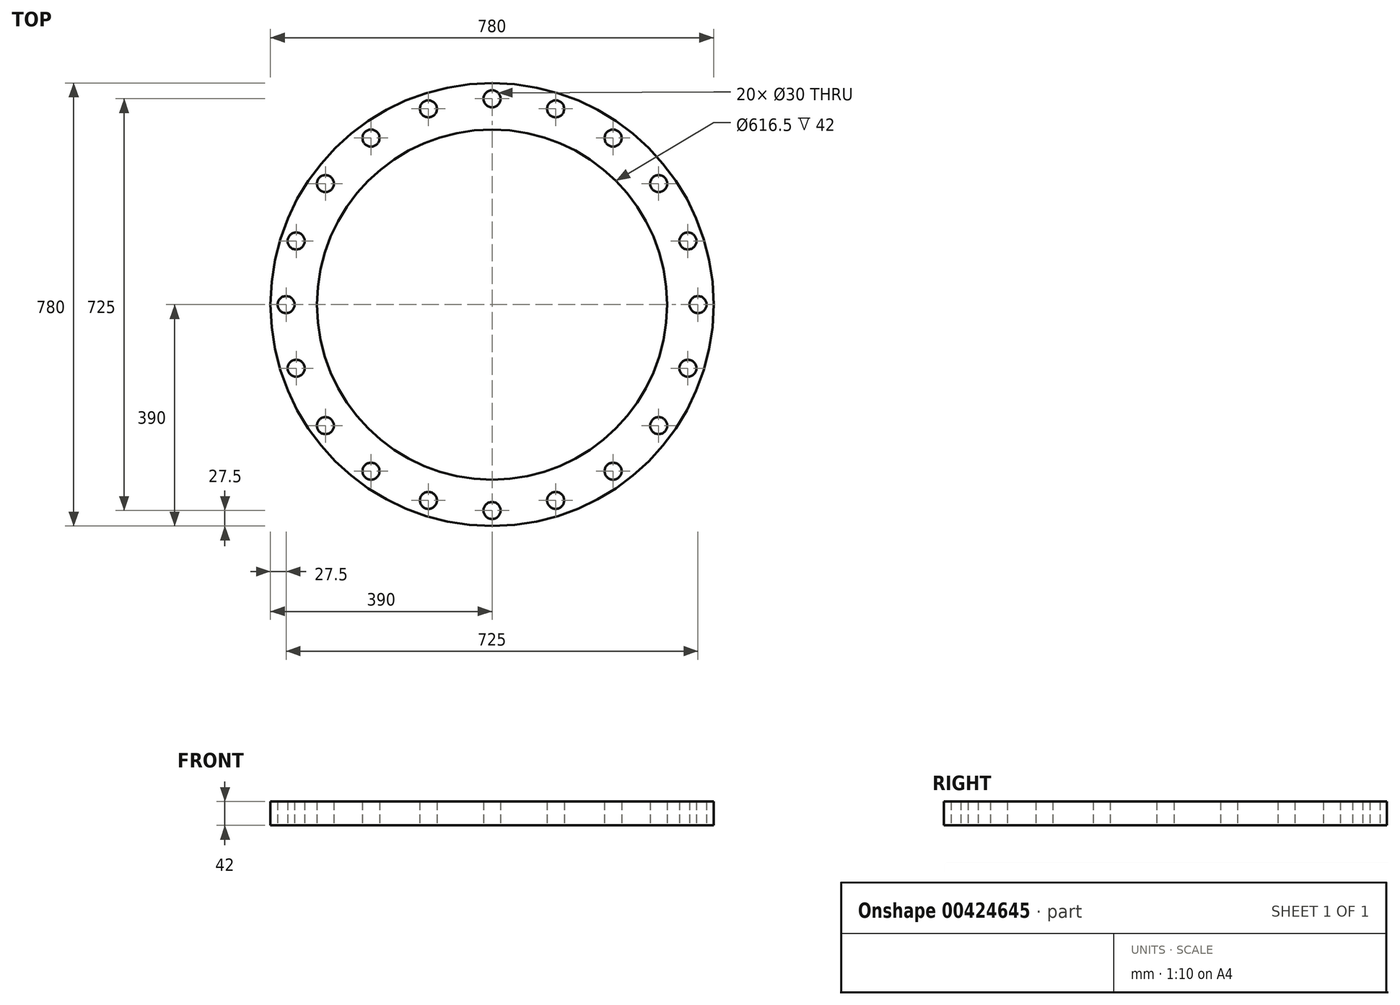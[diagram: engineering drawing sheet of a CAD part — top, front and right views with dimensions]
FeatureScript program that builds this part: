
annotation { "Feature Type Name" : "Feature", "Feature Type Description" : "" }
export const myFeature = defineFeature(function(context is Context, id is Id, definition is map)
    precondition{}
    {
        {
            var Q0;
            Q0=qCreatedBy(makeId("Top.planeOp"),FACE);
            var sketch = newSketch(context, id + "F0", { "sketchPlane" : qUnion([Q0])});
            skCircle(sketch, "E0", {"center": v(0, 0) * mm, "radius": 390 * mm});
            skCircle(sketch, "E1", {"center": v(0, 0) * mm, "radius": 308.25 * mm});
            skCircle(sketch, "E2", {"center": v(362.5, 0) * mm, "radius": 15 * mm});
            skCircle(sketch, "E3.1.0", {"center": v(344.76, 112.02) * mm, "radius": 15 * mm});
            skCircle(sketch, "E3.2.0", {"center": v(293.27, 213.07) * mm, "radius": 15 * mm});
            skCircle(sketch, "E3.3.0", {"center": v(213.07, 293.27) * mm, "radius": 15 * mm});
            skCircle(sketch, "E3.4.0", {"center": v(112.02, 344.76) * mm, "radius": 15 * mm});
            skCircle(sketch, "E3.5.0", {"center": v(0, 362.5) * mm, "radius": 15 * mm});
            skCircle(sketch, "E3.6.0", {"center": v(-112.02, 344.76) * mm, "radius": 15 * mm});
            skCircle(sketch, "E3.7.0", {"center": v(-213.07, 293.27) * mm, "radius": 15 * mm});
            skCircle(sketch, "E3.8.0", {"center": v(-293.27, 213.07) * mm, "radius": 15 * mm});
            skCircle(sketch, "E3.9.0", {"center": v(-344.76, 112.02) * mm, "radius": 15 * mm});
            skCircle(sketch, "E3.10.0", {"center": v(-362.5, 0) * mm, "radius": 15 * mm});
            skCircle(sketch, "E3.11.0", {"center": v(-344.76, -112.02) * mm, "radius": 15 * mm});
            skCircle(sketch, "E3.12.0", {"center": v(-293.27, -213.07) * mm, "radius": 15 * mm});
            skCircle(sketch, "E3.13.0", {"center": v(-213.07, -293.27) * mm, "radius": 15 * mm});
            skCircle(sketch, "E3.14.0", {"center": v(-112.02, -344.76) * mm, "radius": 15 * mm});
            skCircle(sketch, "E3.15.0", {"center": v(0, -362.5) * mm, "radius": 15 * mm});
            skCircle(sketch, "E4.1.16.0", {"center": v(112.02, -344.76) * mm, "radius": 15 * mm});
            skCircle(sketch, "E4.1.17.0", {"center": v(213.07, -293.27) * mm, "radius": 15 * mm});
            skCircle(sketch, "E4.1.18.0", {"center": v(293.27, -213.07) * mm, "radius": 15 * mm});
            skCircle(sketch, "E4.1.19.0", {"center": v(344.76, -112.02) * mm, "radius": 15 * mm});
            skSolve(sketch);
        }
        {
            var Q0;
            Q0=makeQuery(id+"F0.imprint","IMPRINT",FACE,{"disambiguationData":[TD([[makeQuery(id+"F0.imprint","IMPRINT",EDGE,{"derivedFrom":sQuery(id+"F0.wireOp",EDGE,"E0")}),1.0]])]});
            extrude(context, id + "F1", {"entities" : qUnion([Q0]), "depth" : 42 * mm});
        }
    });
